# Revit family: Foam_Soap_Dispenser-Automatic-Bobrick-B-90X_Series
name_source: partatom
category: Specialty Equipment
units: mm (PartAtom-declared; Revit-internal decimal feet)

## family parameters
Always vertical = No
Cut with Voids When Loaded = No
OmniClass Number = 23.40.20.21.34
OmniClass Title = Soap Holders, Dispensers
Part Type = Normal
Room Calculation Point = No
Round Connector Dimension = Use Diameter
Shared = Yes
Work Plane-Based = Yes

## types (5) — shared parameters
6V AC Adapter = Yes
ADA Compliant = Yes
Adapter Voltage = 6V
Assembly Code = C1030210
Bottle System Height = 18 1/2"
Bottom Housing Material = ABS Plastic-Bobrick-Black
Capacity = 34-fl oz (1.0-L).
Counter Top Thickness = 2"
Counter Top Thickness Constraint = 2"
Default Elevation = 0"
Description = Counter-Mounted Automatic Top-Fill Bulk Foam Soap Dispenser
Foam Soap Dispenser = Yes
Height = 3 15/16"
Installation Type = Counter Mounted
Length = 5 9/16"
Model = Bobrick
Mounting Hole Diameter = 1 3/8"
Nozzle Tip Material = ABS-Bobrick-Grey
Soap Bottle Material = Polyethylene-Bobrick-Translucent White
Stem and Funnel Material = Delrin-Bobrick-Red
URL = http://www.bobrick.com
Width = 2 1/16"

## per-type parameters (varying)
| type | Finish | Spout Material |
| B-905 | Cast Zinc-Bobrick-Brushed Nickel | Cast Zinc-Bobrick-Brushed Nickel |
| B-900 | Cast Zinc-Bobrick-Brushed Brass | Cast Zinc-Bobrick-Brushed Brass |
| B-902 | Cast Zinc-Bobrick-Matte Black | Cast Zinc-Bobrick-Matte Black |
| B-908 | Cast Zinc-Bobrick-Polished Chrome | Cast Zinc-Bobrick-Polished Chrome |
| B-901 | Cast Zinc-Bobrick-Polished Graphite | Cast Zinc-Bobrick-Polished Graphite |

note: column(s) folded — value = type name in every type: Manufacturer

## geometry (parser evidence)
native form markers: Sweep x2
no freeform markers — native parametric forms only
